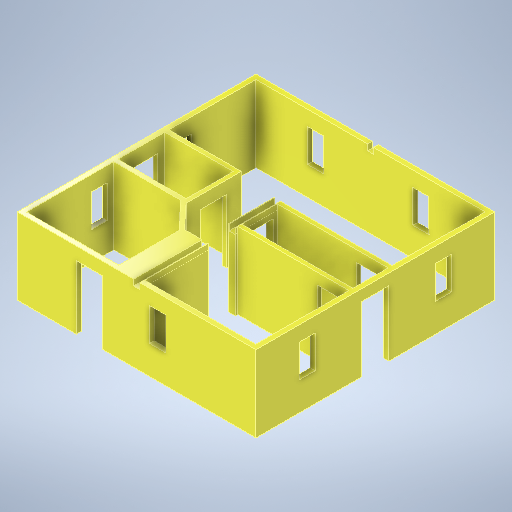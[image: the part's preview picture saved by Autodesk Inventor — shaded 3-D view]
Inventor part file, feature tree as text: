
AUTODESK INVENTOR PART (.ipt)
format: ipt  version: 2025 (Build 290162000, 162)  size: 512,000 bytes
history: native  units: in
note: dims shown in document units (in); Inventor stores cm internally (conversion verified against a paired STEP export)
features: extrude x12, sketch x12
ambient origin geometry x8: Origin, YZ Plane, XZ Plane, XY Plane, X Axis, Y Axis, Z Axis, Center Point
bodies: Solid1 (feature_tree)
feature tree (24):
  extrude  "Extrusion1"  Depth=41.0in
  extrude  "Extrusion3"  Depth=90.75in
  extrude  "Extrusion5"  Depth=20.0in
  extrude  "Extrusion6"  Depth=36.0in
  extrude  "Extrusion7"  Depth=33.0in
  extrude  "Extrusion11"  Depth=12.0in
  extrude  "Extrusion12"  Depth=36.0in
  extrude  "Extrusion13"  Depth=41.0in TaperAngle=0.0deg
  extrude  "Extrusion14"  Depth=34.0in
  extrude  "Extrusion15"  Depth=80.0in TaperAngle=0.0deg
  extrude  "Extrusion16"  Depth=18.3813in
  extrude  "Extrusion17"  Depth=7.5in TaperAngle=0.0deg
  sketch  "Sketch1"  dims[d14=96.0in d15=0.0in d78=41.0in]
  sketch  "Sketch3"  dims[d79=20.0in d81=90.75in]
  sketch  "Sketch5"  dims[d82=41.0in d83=20.0in]
  sketch  "Sketch6"  dims[d84=36.0in d85=36.0in]
  sketch  "Sketch7"  dims[d86=1.0in d87=0.0in d102=33.0in]
  sketch  "Sketch11"  dims[d103=80.0in d104=12.0in]
  sketch  "Sketch12"  dims[d105=20.0in d106=36.0in]
  sketch  "Sketch13"  dims[d107=41.0in d108=1.0in d109=0.0in]
  sketch  "Sketch14"  dims[d114=68.375in d115=34.0in]
  sketch  "Sketch15"  dims[d117=80.0in d118=1.0in d119=0.0in]
  sketch  "Sketch16"  dims[d120=33.0in d121=18.3813in]
  sketch  "Sketch17"  dims[d122=80.0in d123=1.0in d124=0.0in d153=300.0in d154=5.875in d156=109.25in d157=109.5in d160=90.75in d161=58.75in d164=85.75in d165=59.0in d166=5.875in d167=288.0in d168=84.0in d169=116.0in d170=75.5in d175=5.0in d180=5.0in d181=3.0in d183=117.0in d184=117.0in d186=80.0in d187=36.0in d189=41.0in d190=41.0in d191=8.875in d192=96.0in d193=0.0in d194=8.25in d195=41.0in d196=36.0in d197=20.0in d198=8.25in d199=20.0in d200=41.0in d201=36.0in d202=1.0in d203=0.0in d204=34.0in d205=5.125in d206=82.0in d207=1.0in d208=0.0in d210=20.0in d212=41.0in d214=48.5in d216=36.0in d218=41.0in d219=20.0in d220=48.5in d221=36.0in d222=1.0in d223=0.0in d224=5.125in d225=34.0in d226=82.0in d227=1.0in d228=0.0in d229=5.5in d230=34.0in d231=82.0in d232=1.0in d233=0.0in d234=90.75in d235=6.345in d236=7.5in d237=150.0in d238=49.0in d239=8.75in d240=7.5in d241=0.0in]
